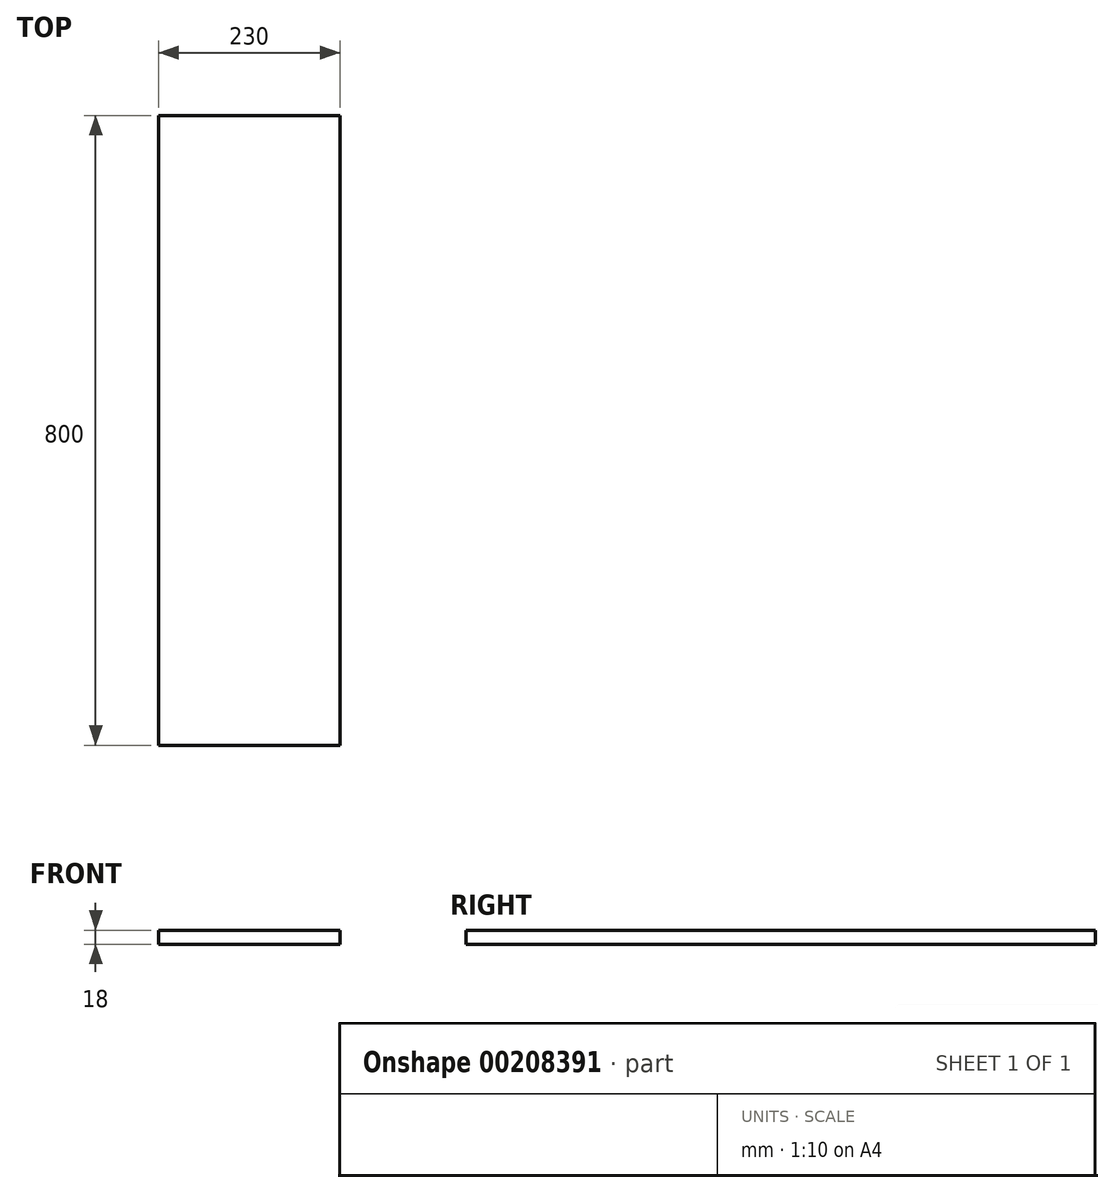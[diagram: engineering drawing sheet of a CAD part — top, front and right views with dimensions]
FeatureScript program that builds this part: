
annotation { "Feature Type Name" : "Feature", "Feature Type Description" : "" }
export const myFeature = defineFeature(function(context is Context, id is Id, definition is map)
    precondition{}
    {
        {
            var Q0;
            Q0=qCreatedBy(makeId("Front.planeOp"),FACE);
            var sketch = newSketch(context, id + "F0", { "sketchPlane" : qUnion([Q0])});
            skLineSegment(sketch, "E0.bottom", {"start": v(-98, 9.5) * mm, "end": v(132, 9.5) * mm});
            skLineSegment(sketch, "E0.top", {"start": v(-98, -8.5) * mm, "end": v(132, -8.5) * mm});
            skLineSegment(sketch, "E0.left", {"start": v(-98, 9.5) * mm, "end": v(-98, -8.5) * mm});
            skLineSegment(sketch, "E0.right", {"start": v(132, 9.5) * mm, "end": v(132, -8.5) * mm});
            skSolve(sketch);
        }
        {
            var Q0;
            Q0=makeQuery(id+"F0.imprint","IMPRINT",FACE,{"disambiguationData":[TD([[makeQuery(id+"F0.imprint","IMPRINT",EDGE,{"derivedFrom":sQuery(id+"F0.wireOp",EDGE,"E0.bottom")}),-1.0]])]});
            extrude(context, id + "F1", {"entities" : qUnion([Q0]), "oppositeDirection" : true, "depth" : 800 * mm});
        }
    });
